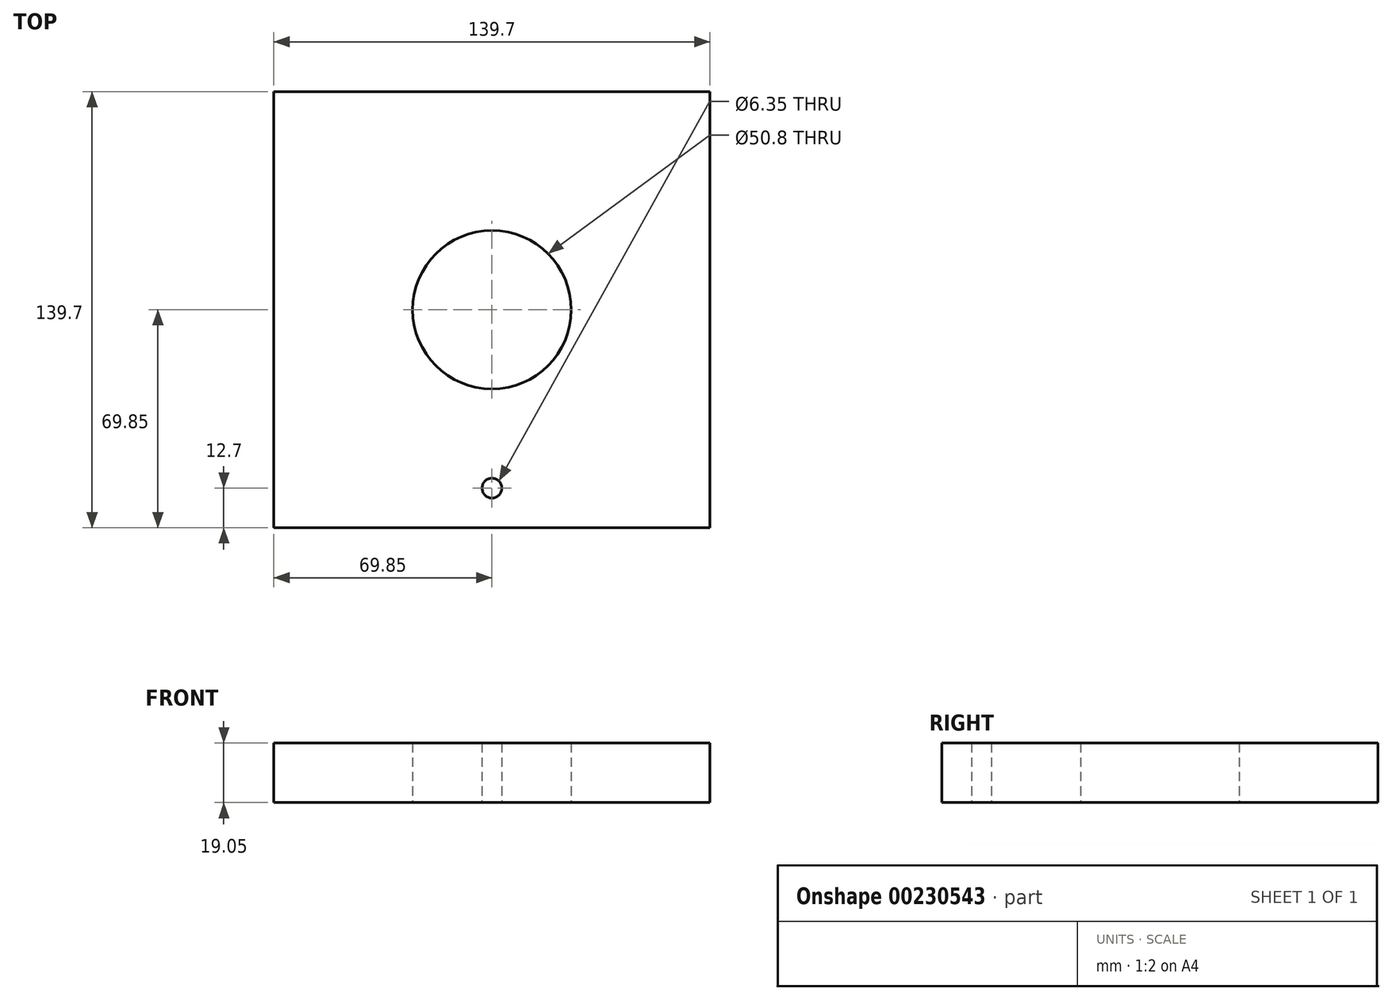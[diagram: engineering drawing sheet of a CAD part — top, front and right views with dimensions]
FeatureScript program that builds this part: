
annotation { "Feature Type Name" : "Feature", "Feature Type Description" : "" }
export const myFeature = defineFeature(function(context is Context, id is Id, definition is map)
    precondition{}
    {
        {
            var Q0;
            Q0=qCreatedBy(makeId("Top.planeOp"),FACE);
            var sketch = newSketch(context, id + "F0", { "sketchPlane" : qUnion([Q0])});
            skLineSegment(sketch, "E0.bottom", {"start": v(-69.85, 69.85) * mm, "end": v(69.85, 69.85) * mm});
            skLineSegment(sketch, "E0.top", {"start": v(-69.85, -69.85) * mm, "end": v(69.85, -69.85) * mm});
            skLineSegment(sketch, "E0.left", {"start": v(-69.85, 69.85) * mm, "end": v(-69.85, -69.85) * mm});
            skLineSegment(sketch, "E0.right", {"start": v(69.85, 69.85) * mm, "end": v(69.85, -69.85) * mm});
            skPoint(sketch, "E0.middle", {"position": v(0, 0) * mm});
            skPoint(sketch, "E1.endSnap0", {"position": v(0, -69.85) * mm});
            skLineSegment(sketch, "E2", {"start": v(0, -69.85) * mm, "end": v(0, -57.15) * mm});
            skLineSegment(sketch, "E3", {"start": v(0, -57.15) * mm, "end": v(0, -19.05) * mm});
            skCircle(sketch, "E4", {"center": v(0, -57.15) * mm, "radius": 3.18 * mm});
            skCircle(sketch, "E5", {"center": v(0, 0) * mm, "radius": 25.4 * mm});
            skSolve(sketch);
        }
        {
            var Q0;
            Q0=makeQuery(id+"F0.imprint","IMPRINT",FACE,{"disambiguationData":[TD([[makeQuery(id+"F0.imprint","IMPRINT",EDGE,{"derivedFrom":sQuery(id+"F0.wireOp",EDGE,"E0.bottom")}),-1.0]])]});
            extrude(context, id + "F1", {"entities" : qUnion([Q0]), "depth" : 19.05 * mm});
        }
    });
